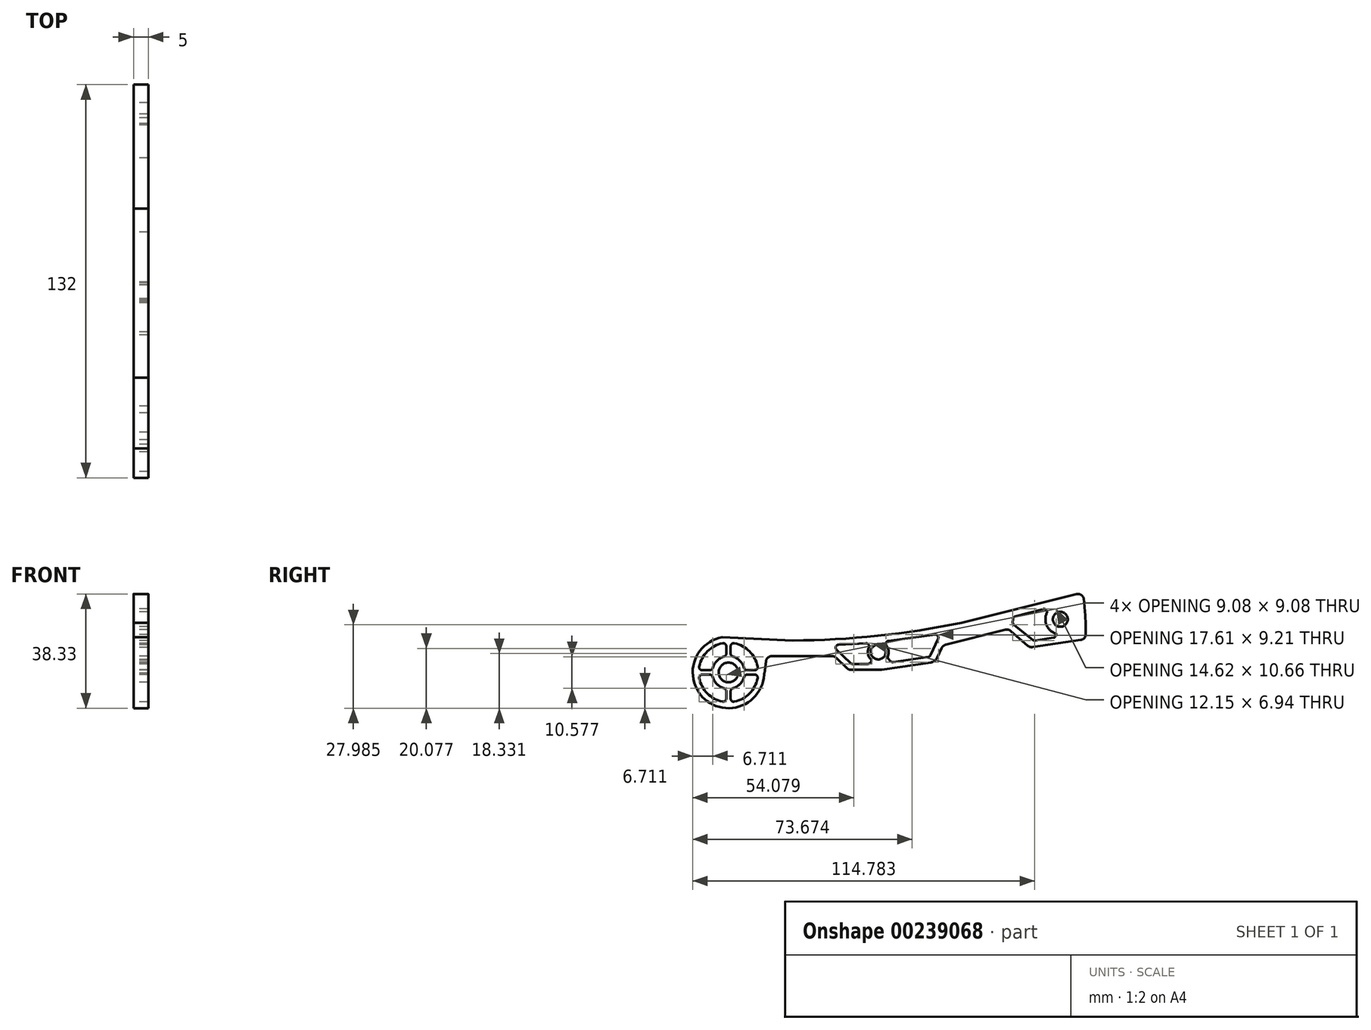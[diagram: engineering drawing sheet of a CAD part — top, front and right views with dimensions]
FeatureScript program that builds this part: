
annotation { "Feature Type Name" : "Feature", "Feature Type Description" : "" }
export const myFeature = defineFeature(function(context is Context, id is Id, definition is map)
    precondition{}
    {
        {
            var Q0;
            Q0=qCreatedBy(makeId("Right.planeOp"),FACE);
            var sketch = newSketch(context, id + "F0", { "sketchPlane" : qUnion([Q0])});
            skArc(sketch, "E0", {"start": v(21.96, 10.72) * mm, "mid": v(21.96, 10.73) * mm, "end": v(21.96, 10.73) * mm});
            skArc(sketch, "E1", {"start": v(120, 12.9) * mm, "mid": v(119.81, 18.73) * mm, "end": v(119.34, 24.54) * mm});
            skArc(sketch, "E2", {"start": v(21.46, 10.73) * mm, "mid": v(22.07, 10.72) * mm, "end": v(22.67, 10.8) * mm});
            skLineSegment(sketch, "E3", {"start": v(21.83, 10.72) * mm, "end": v(-2.06, 11.82) * mm});
            skLineSegment(sketch, "E4", {"start": v(78.34, 16.72) * mm, "end": v(116.87, 26.27) * mm});
            skCircle(sketch, "E5", {"center": v(0, 0) * mm, "radius": 3.3 * mm});
            skPoint(sketch, "E6.orphan", {"position": v(21.83, 9.28) * mm});
            skArc(sketch, "E7", {"start": v(21.58, 10.73) * mm, "mid": v(50.11, 12.3) * mm, "end": v(78.34, 16.72) * mm});
            skCircle(sketch, "E8", {"center": v(111.43, 17.83) * mm, "radius": 2.5 * mm});
            skCircle(sketch, "E9", {"center": v(50.3, 6.86) * mm, "radius": 2.5 * mm});
            skArc(sketch, "E10", {"start": v(-2.06, 11.82) * mm, "mid": v(-7.99, -8.95) * mm, "end": v(11.98, -0.7) * mm});
            skLineSegment(sketch, "E11", {"start": v(118.3, 10.9) * mm, "end": v(102.16, 8.49) * mm});
            skLineSegment(sketch, "E12", {"start": v(51.16, 0.86) * mm, "end": v(41.18, 0.86) * mm});
            skPoint(sketch, "E13.visualSharp", {"position": v(11.97, 0.86) * mm});
            skArc(sketch, "E13.filletArc", {"start": v(12.07, -0.27) * mm, "mid": v(12, -0.48) * mm, "end": v(11.98, -0.7) * mm});
            skLineSegment(sketch, "E14", {"start": v(14.57, 5.48) * mm, "end": v(34.75, 5.48) * mm});
            skLineSegment(sketch, "E15", {"start": v(72.85, 9.24) * mm, "end": v(93, 14.35) * mm});
            skLineSegment(sketch, "E16", {"start": v(12.58, 3.74) * mm, "end": v(11.97, -1.01) * mm});
            skLineSegment(sketch, "E17", {"start": v(36.13, 4.93) * mm, "end": v(39.8, 1.42) * mm});
            skLineSegment(sketch, "E18", {"start": v(70.01, 4.85) * mm, "end": v(71.53, 8.13) * mm});
            skLineSegment(sketch, "E19", {"start": v(94.8, 13.92) * mm, "end": v(100.56, 8.95) * mm});
            skLineSegment(sketch, "E20.trimOffspring", {"start": v(68.04, 3.37) * mm, "end": v(51.45, 0.89) * mm});
            skPoint(sketch, "E21.visualSharp", {"position": v(119.08, 26.82) * mm});
            skArc(sketch, "E21.filletArc", {"start": v(119.34, 24.54) * mm, "mid": v(118.5, 25.97) * mm, "end": v(116.87, 26.27) * mm});
            skPoint(sketch, "E22.visualSharp", {"position": v(120, 11.16) * mm});
            skArc(sketch, "E22.filletArc", {"start": v(118.3, 10.9) * mm, "mid": v(119.52, 11.58) * mm, "end": v(120, 12.9) * mm});
            skPoint(sketch, "E23.visualSharp", {"position": v(101.25, 8.35) * mm});
            skArc(sketch, "E23.filletArc", {"start": v(100.56, 8.95) * mm, "mid": v(101.3, 8.54) * mm, "end": v(102.16, 8.49) * mm});
            skPoint(sketch, "E24.visualSharp", {"position": v(94.01, 14.6) * mm});
            skArc(sketch, "E24.filletArc", {"start": v(94.8, 13.92) * mm, "mid": v(93.95, 14.35) * mm, "end": v(93, 14.35) * mm});
            skArc(sketch, "E25.filletArc", {"start": v(72.85, 9.24) * mm, "mid": v(72.06, 8.84) * mm, "end": v(71.53, 8.13) * mm});
            skArc(sketch, "E26.filletArc", {"start": v(68.04, 3.37) * mm, "mid": v(69.22, 3.86) * mm, "end": v(70.01, 4.85) * mm});
            skArc(sketch, "E27.filletArc", {"start": v(39.8, 1.42) * mm, "mid": v(40.43, 1) * mm, "end": v(41.18, 0.86) * mm});
            skArc(sketch, "E28.filletArc", {"start": v(36.13, 4.93) * mm, "mid": v(35.5, 5.34) * mm, "end": v(34.75, 5.48) * mm});
            skPoint(sketch, "E29.visualSharp", {"position": v(12.8, 5.48) * mm});
            skArc(sketch, "E29.filletArc", {"start": v(14.57, 5.48) * mm, "mid": v(13.25, 4.99) * mm, "end": v(12.58, 3.74) * mm});
            skPoint(sketch, "E30.visualSharp", {"position": v(51.3, 0.86) * mm});
            skArc(sketch, "E30.filletArc", {"start": v(51.16, 0.86) * mm, "mid": v(51.3, 0.87) * mm, "end": v(51.45, 0.89) * mm});
            skArc(sketch, "E31", {"start": v(1.94, -9.8) * mm, "mid": v(7.07, -7.07) * mm, "end": v(9.8, -1.94) * mm});
            skArc(sketch, "E32", {"start": v(1.48, -5.3) * mm, "mid": v(3.89, -3.89) * mm, "end": v(5.3, -1.48) * mm});
            skArc(sketch, "E33", {"start": v(10.03, 0.75) * mm, "mid": v(10, 0.75) * mm, "end": v(9.97, 0.75) * mm});
            skLineSegment(sketch, "E34", {"start": v(-8.83, 0.75) * mm, "end": v(-6.26, 0.75) * mm});
            skLineSegment(sketch, "E35", {"start": v(-8.83, -0.75) * mm, "end": v(-6.26, -0.75) * mm});
            skLineSegment(sketch, "E36", {"start": v(-0.75, 8.83) * mm, "end": v(-0.75, 6.26) * mm});
            skLineSegment(sketch, "E37", {"start": v(0.75, 8.83) * mm, "end": v(0.75, 6.26) * mm});
            skPoint(sketch, "E38.center.orphan", {"position": v(0, -10) * mm});
            skPoint(sketch, "E39.center.orphan", {"position": v(0, 10) * mm});
            skArc(sketch, "E40.trimOffspring", {"start": v(-1.94, 9.8) * mm, "mid": v(-7.07, 7.07) * mm, "end": v(-9.8, 1.94) * mm});
            skPoint(sketch, "E41.center.orphan", {"position": v(-10, 0) * mm});
            skArc(sketch, "E42.trimOffspring", {"start": v(-9.8, -1.94) * mm, "mid": v(-7.07, -7.07) * mm, "end": v(-1.94, -9.8) * mm});
            skArc(sketch, "E43.trimOffspring", {"start": v(9.8, 1.94) * mm, "mid": v(7.07, 7.07) * mm, "end": v(1.94, 9.8) * mm});
            skLineSegment(sketch, "E44.trimOffspring", {"start": v(6.26, -0.75) * mm, "end": v(8.83, -0.75) * mm});
            skLineSegment(sketch, "E45.trimOffspring", {"start": v(6.26, 0.75) * mm, "end": v(8.83, 0.75) * mm});
            skLineSegment(sketch, "E46.trimOffspring", {"start": v(0.75, -6.26) * mm, "end": v(0.75, -8.83) * mm});
            skLineSegment(sketch, "E47.trimOffspring", {"start": v(-0.75, -6.26) * mm, "end": v(-0.75, -8.83) * mm});
            skArc(sketch, "E48.trimOffspring", {"start": v(5.3, 1.48) * mm, "mid": v(3.89, 3.89) * mm, "end": v(1.48, 5.3) * mm});
            skArc(sketch, "E49.trimOffspring", {"start": v(-1.48, 5.3) * mm, "mid": v(-3.89, 3.89) * mm, "end": v(-5.3, 1.48) * mm});
            skArc(sketch, "E50.trimOffspring", {"start": v(-5.3, -1.48) * mm, "mid": v(-3.89, -3.89) * mm, "end": v(-1.48, -5.3) * mm});
            skArc(sketch, "E51.filletArc", {"start": v(8.83, 0.75) * mm, "mid": v(9.6, 1.11) * mm, "end": v(9.8, 1.94) * mm});
            skPoint(sketch, "E52.visualSharp", {"position": v(0.75, 9.97) * mm});
            skArc(sketch, "E52.filletArc", {"start": v(1.94, 9.8) * mm, "mid": v(1.11, 9.6) * mm, "end": v(0.75, 8.83) * mm});
            skPoint(sketch, "E53.visualSharp", {"position": v(0.75, 5.45) * mm});
            skArc(sketch, "E53.filletArc", {"start": v(0.75, 6.26) * mm, "mid": v(0.95, 5.66) * mm, "end": v(1.48, 5.3) * mm});
            skPoint(sketch, "E54.visualSharp", {"position": v(5.45, 0.75) * mm});
            skArc(sketch, "E54.filletArc", {"start": v(5.3, 1.48) * mm, "mid": v(5.66, 0.95) * mm, "end": v(6.26, 0.75) * mm});
            skPoint(sketch, "E55.visualSharp", {"position": v(5.45, -0.75) * mm});
            skArc(sketch, "E55.filletArc", {"start": v(6.26, -0.75) * mm, "mid": v(5.66, -0.95) * mm, "end": v(5.3, -1.48) * mm});
            skPoint(sketch, "E56.visualSharp", {"position": v(9.97, -0.75) * mm});
            skArc(sketch, "E56.filletArc", {"start": v(9.8, -1.94) * mm, "mid": v(9.6, -1.11) * mm, "end": v(8.83, -0.75) * mm});
            skPoint(sketch, "E57.visualSharp", {"position": v(0.75, -5.45) * mm});
            skArc(sketch, "E57.filletArc", {"start": v(1.48, -5.3) * mm, "mid": v(0.95, -5.66) * mm, "end": v(0.75, -6.26) * mm});
            skPoint(sketch, "E58.visualSharp", {"position": v(0.75, -9.97) * mm});
            skArc(sketch, "E58.filletArc", {"start": v(0.75, -8.83) * mm, "mid": v(1.11, -9.6) * mm, "end": v(1.94, -9.8) * mm});
            skPoint(sketch, "E59.visualSharp", {"position": v(-0.75, -9.97) * mm});
            skArc(sketch, "E59.filletArc", {"start": v(-1.94, -9.8) * mm, "mid": v(-1.12, -9.6) * mm, "end": v(-0.75, -8.83) * mm});
            skPoint(sketch, "E60.visualSharp", {"position": v(-0.75, -5.45) * mm});
            skArc(sketch, "E60.filletArc", {"start": v(-0.75, -6.26) * mm, "mid": v(-0.95, -5.66) * mm, "end": v(-1.48, -5.3) * mm});
            skPoint(sketch, "E61.visualSharp", {"position": v(-5.45, -0.75) * mm});
            skArc(sketch, "E61.filletArc", {"start": v(-5.3, -1.48) * mm, "mid": v(-5.66, -0.95) * mm, "end": v(-6.26, -0.75) * mm});
            skPoint(sketch, "E62.visualSharp", {"position": v(-9.97, -0.75) * mm});
            skArc(sketch, "E62.filletArc", {"start": v(-8.83, -0.75) * mm, "mid": v(-9.6, -1.11) * mm, "end": v(-9.8, -1.94) * mm});
            skPoint(sketch, "E63.visualSharp", {"position": v(-9.97, 0.75) * mm});
            skArc(sketch, "E63.filletArc", {"start": v(-9.8, 1.94) * mm, "mid": v(-9.6, 1.11) * mm, "end": v(-8.83, 0.75) * mm});
            skPoint(sketch, "E64.visualSharp", {"position": v(-5.45, 0.75) * mm});
            skArc(sketch, "E64.filletArc", {"start": v(-6.26, 0.75) * mm, "mid": v(-5.66, 0.95) * mm, "end": v(-5.3, 1.48) * mm});
            skPoint(sketch, "E65.visualSharp", {"position": v(-0.75, 5.45) * mm});
            skArc(sketch, "E65.filletArc", {"start": v(-1.48, 5.3) * mm, "mid": v(-0.95, 5.66) * mm, "end": v(-0.75, 6.26) * mm});
            skPoint(sketch, "E66.visualSharp", {"position": v(-0.75, 9.97) * mm});
            skArc(sketch, "E66.filletArc", {"start": v(-0.75, 8.83) * mm, "mid": v(-1.11, 9.6) * mm, "end": v(-1.94, 9.8) * mm});
            skArc(sketch, "E67", {"start": v(47.15, 8.37) * mm, "mid": v(46.9, 6.05) * mm, "end": v(48.15, 4.1) * mm});
            skLineSegment(sketch, "E68", {"start": v(55.3, 3.48) * mm, "end": v(67.13, 5.26) * mm});
            skLineSegment(sketch, "E69", {"start": v(46.82, 2.86) * mm, "end": v(41.59, 2.86) * mm});
            skLineSegment(sketch, "E70", {"start": v(67.89, 5.83) * mm, "end": v(70.4, 11.27) * mm});
            skPoint(sketch, "E71.orphan", {"position": v(54.41, 2.86) * mm});
            skPoint(sketch, "E72.orphan", {"position": v(71.9, 13.02) * mm});
            skPoint(sketch, "E73.orphan", {"position": v(71.9, 14.56) * mm});
            skLineSegment(sketch, "E74.trimOffspring", {"start": v(53.73, 10.6) * mm, "end": v(69.35, 12.68) * mm});
            skLineSegment(sketch, "E75", {"start": v(47.67, 3.33) * mm, "end": v(48.15, 4.1) * mm});
            skLineSegment(sketch, "E76", {"start": v(54.45, 3.75) * mm, "end": v(53.76, 4.41) * mm});
            skArc(sketch, "E77.trimOffspring", {"start": v(53.54, 5.52) * mm, "mid": v(53.77, 7.32) * mm, "end": v(53.07, 9) * mm});
            skPoint(sketch, "E78.visualSharp", {"position": v(51.13, 10.26) * mm});
            skArc(sketch, "E78.filletArc", {"start": v(53.73, 10.6) * mm, "mid": v(52.94, 10) * mm, "end": v(53.07, 9) * mm});
            skPoint(sketch, "E79.visualSharp", {"position": v(53.23, 4.93) * mm});
            skArc(sketch, "E79.filletArc", {"start": v(53.54, 5.52) * mm, "mid": v(53.48, 4.93) * mm, "end": v(53.76, 4.41) * mm});
            skPoint(sketch, "E80.visualSharp", {"position": v(54.8, 3.4) * mm});
            skArc(sketch, "E80.filletArc", {"start": v(54.45, 3.75) * mm, "mid": v(54.84, 3.52) * mm, "end": v(55.3, 3.48) * mm});
            skPoint(sketch, "E81.visualSharp", {"position": v(67.66, 5.34) * mm});
            skArc(sketch, "E81.filletArc", {"start": v(67.13, 5.26) * mm, "mid": v(67.58, 5.45) * mm, "end": v(67.89, 5.83) * mm});
            skPoint(sketch, "E82.visualSharp", {"position": v(71.15, 12.92) * mm});
            skArc(sketch, "E82.filletArc", {"start": v(70.4, 11.27) * mm, "mid": v(70.29, 12.28) * mm, "end": v(69.35, 12.68) * mm});
            skLineSegment(sketch, "E83", {"start": v(40.89, 3.15) * mm, "end": v(36.3, 7.61) * mm});
            skPoint(sketch, "E84.visualSharp", {"position": v(34.64, 9.23) * mm});
            skArc(sketch, "E84.filletArc", {"start": v(36.96, 9.33) * mm, "mid": v(36.07, 8.68) * mm, "end": v(36.3, 7.61) * mm});
            skArc(sketch, "E85.filletArc", {"start": v(40.89, 3.15) * mm, "mid": v(41.2, 2.94) * mm, "end": v(41.59, 2.86) * mm});
            skPoint(sketch, "E86.visualSharp", {"position": v(47.38, 2.86) * mm});
            skArc(sketch, "E86.filletArc", {"start": v(46.82, 2.86) * mm, "mid": v(47.3, 2.99) * mm, "end": v(47.67, 3.33) * mm});
            skLineSegment(sketch, "E87", {"start": v(36.96, 9.33) * mm, "end": v(46.2, 9.8) * mm});
            skPoint(sketch, "E88.visualSharp", {"position": v(48.62, 9.92) * mm});
            skArc(sketch, "E88.filletArc", {"start": v(47.15, 8.37) * mm, "mid": v(47.08, 9.36) * mm, "end": v(46.2, 9.8) * mm});
            skArc(sketch, "E89", {"start": v(106.87, 19.9) * mm, "mid": v(106.86, 15.79) * mm, "end": v(109.94, 13.06) * mm});
            skLineSegment(sketch, "E90", {"start": v(96.28, 18.78) * mm, "end": v(105.7, 21.28) * mm});
            skLineSegment(sketch, "E91", {"start": v(102.33, 10.87) * mm, "end": v(95.85, 15.98) * mm});
            skLineSegment(sketch, "E92", {"start": v(95.54, 17.88) * mm, "end": v(95.47, 16.82) * mm});
            skLineSegment(sketch, "E93", {"start": v(110.09, 12.8) * mm, "end": v(110, 12.43) * mm});
            skLineSegment(sketch, "E94.trimOffspring", {"start": v(109.19, 11.67) * mm, "end": v(103.1, 10.67) * mm});
            skPoint(sketch, "E95.visualSharp", {"position": v(95.58, 18.6) * mm});
            skArc(sketch, "E95.filletArc", {"start": v(96.28, 18.78) * mm, "mid": v(95.76, 18.45) * mm, "end": v(95.54, 17.88) * mm});
            skPoint(sketch, "E96.visualSharp", {"position": v(95.44, 16.3) * mm});
            skArc(sketch, "E96.filletArc", {"start": v(95.47, 16.82) * mm, "mid": v(95.56, 16.35) * mm, "end": v(95.85, 15.98) * mm});
            skPoint(sketch, "E97.visualSharp", {"position": v(102.67, 10.6) * mm});
            skArc(sketch, "E97.filletArc", {"start": v(102.33, 10.87) * mm, "mid": v(102.7, 10.69) * mm, "end": v(103.1, 10.67) * mm});
            skArc(sketch, "E98.filletArc", {"start": v(109.19, 11.67) * mm, "mid": v(109.7, 11.93) * mm, "end": v(110, 12.43) * mm});
            skPoint(sketch, "E99.visualSharp", {"position": v(110.13, 13) * mm});
            skArc(sketch, "E99.filletArc", {"start": v(110.09, 12.8) * mm, "mid": v(110.06, 12.96) * mm, "end": v(109.94, 13.06) * mm});
            skArc(sketch, "E100.filletArc", {"start": v(106.87, 19.9) * mm, "mid": v(106.73, 20.96) * mm, "end": v(105.7, 21.28) * mm});
            skSolve(sketch);
        }
        {
            var Q0;
            {var subQ0=sQuery(id+"F0.wireOp",EDGE,"E0");Q0=makeQuery(id+"F0.imprint","IMPRINT",FACE,{"disambiguationData":[TD([[makeQuery(id+"F0.imprint","IMPRINT",EDGE,{"derivedFrom":subQ0}),-1.0]])]});}
            var Q1;
            {var subQ0=sQuery(id+"F0.wireOp",EDGE,"E3");var subQ1=sQuery(id+"F0.wireOp",EDGE,"E2");var subQ2=makeQuery(id+"F0.imprint","INTERSECT",VERTEX,{"disambiguationData":[OD(0.0)],"derivedFrom":[subQ1,subQ0]});Q1=makeQuery(id+"F0.imprint","IMPRINT",FACE,{"disambiguationData":[TD([[makeQuery(id+"F0.imprint","IMPRINT",EDGE,{"disambiguationData":[TD([[subQ2,-1.0]])],"derivedFrom":subQ1}),1.0]])]});}
            var Q2;
            {var subQ0=sQuery(id+"F0.wireOp",EDGE,"E0");Q2=makeQuery(id+"F0.imprint","IMPRINT",FACE,{"disambiguationData":[TD([[makeQuery(id+"F0.imprint","IMPRINT",EDGE,{"derivedFrom":subQ0}),1.0]])]});}
            var Q3;
            Q3=makeQuery(id+"F0.imprint","IMPRINT",FACE,{"disambiguationData":[TD([[makeQuery(id+"F0.imprint","IMPRINT",EDGE,{"derivedFrom":sQuery(id+"F0.wireOp",EDGE,"E1")}),1.0]])]});
            extrude(context, id + "F1", {"entities" : qUnion([Q0, Q1, Q2, Q3]), "depth" : 5 * mm});
        }
    });
